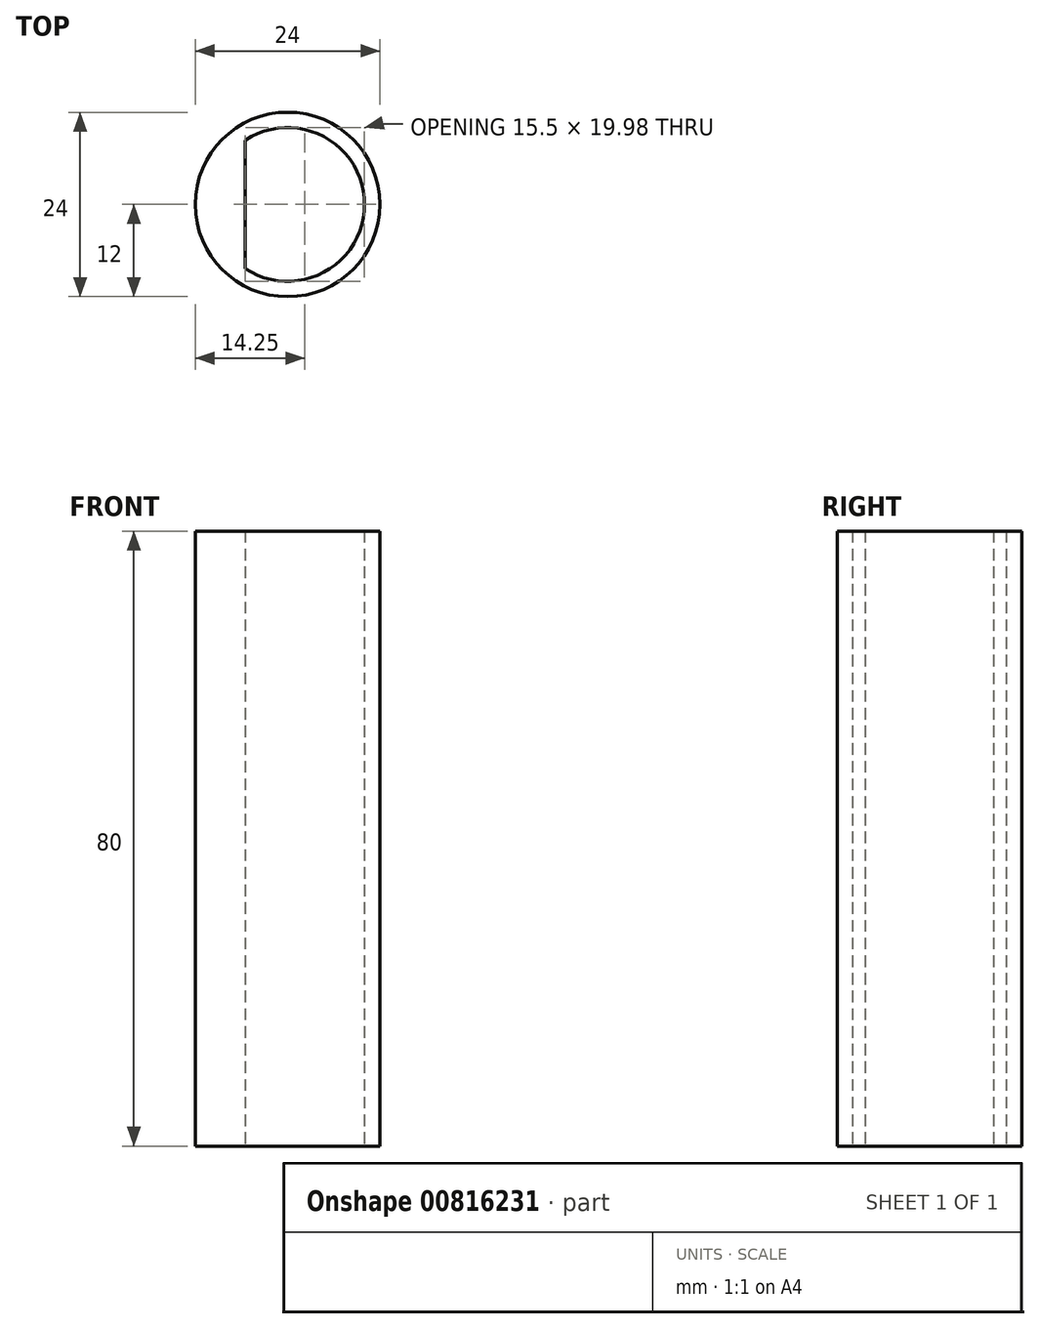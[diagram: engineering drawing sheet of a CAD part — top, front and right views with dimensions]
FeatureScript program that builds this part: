
annotation { "Feature Type Name" : "Feature", "Feature Type Description" : "" }
export const myFeature = defineFeature(function(context is Context, id is Id, definition is map)
    precondition{}
    {
        {
            var Q0;
            Q0=qCreatedBy(makeId("Top.planeOp"),FACE);
            var sketch = newSketch(context, id + "F0", { "sketchPlane" : qUnion([Q0])});
            skCircle(sketch, "E0", {"center": v(0, 0) * mm, "radius": 12 * mm});
            skCircle(sketch, "E1", {"center": v(0, 0) * mm, "radius": 10 * mm});
            skPoint(sketch, "E2", {"position": v(-5.5, 0) * mm});
            skLineSegment(sketch, "E3", {"start": v(-5.5, 8.35) * mm, "end": v(-5.5, -8.35) * mm});
            skSolve(sketch);
        }
        {
            var Q0;
            Q0=makeQuery(id+"F0.imprint","IMPRINT",FACE,{"disambiguationData":[TD([[makeQuery(id+"F0.imprint","IMPRINT",EDGE,{"derivedFrom":sQuery(id+"F0.wireOp",EDGE,"E0")}),1.0]])]});
            var Q1;
            {var subQ0=sQuery(id+"F0.wireOp",EDGE,"E3");Q1=makeQuery(id+"F0.imprint","IMPRINT",FACE,{"disambiguationData":[TD([[makeQuery(id+"F0.imprint","IMPRINT",EDGE,{"derivedFrom":subQ0}),-1.0]])]});}
            extrude(context, id + "F1", {"entities" : qUnion([Q0, Q1]), "depth" : 80 * mm, "offsetDistance" : 25 * mm});
        }
    });
